# Revit family: Accessory-Towel_Bar-KOHLER-Purist-K-14435
name_source: partatom
category: Generic Models
revit_build: Autodesk Revit 2015 (Build: 20140606_1530(x64)
units: mm (PartAtom-declared; Revit-internal decimal feet)

## types (6) — shared parameters
ADA = No
Assembly Code = C1030200
Date Modified = 11/22/2017
Default Elevation = 42"
Description = 18inch towel bar
Height = 3 7/32"
Length = 19 7/8"
Manufacturer = KOHLER Co.
MasterFormat 1995 = 10820
MasterFormat 2004 = 10.28.13
Material = Solid Brass Construction
Product Documentation Link = http://www.us.kohler.com
Product Name = Purist
Product Page URL = http://www.us.kohler.com
URL = https://www.us.kohler.com
Width = 1 7/8"

## per-type parameters (varying)
| type | Finish | Model | Type |
| CP-Polished Chrome | Kohler-Metal-CP-Polished_Chrome | K-14435-CP | 1 |
| SN-Vibrant Polished Nickel | Kohler-Metal-SN-Vibrant_Polished_Nickel | K-14435-SN | 2 |
| BGD-Vibrant Moderne Brushed Gold | Kohler-Metal-BGD-Vibrant_Moderne_Brushed_Gold | K-14435-BGD | 3 |
| BN-Vibrant Brushed Nickel | Kohler-Metal-BN-Vibrant_Brushed_Nickel | K-14435-BN | 4 |
| BV-Vibrant Brushed Bronze | Kohler-Metal-BV-Brushed_Bronze | K-14435-BV | 5 |
| RGD-Vibrant Rose Gold | Kohler-Metal-RGD-Polished_Rose_Gold | K-14435-RGD | 6 |

## geometry (parser evidence)
native form markers: Sweep x6
no freeform markers — native parametric forms only
